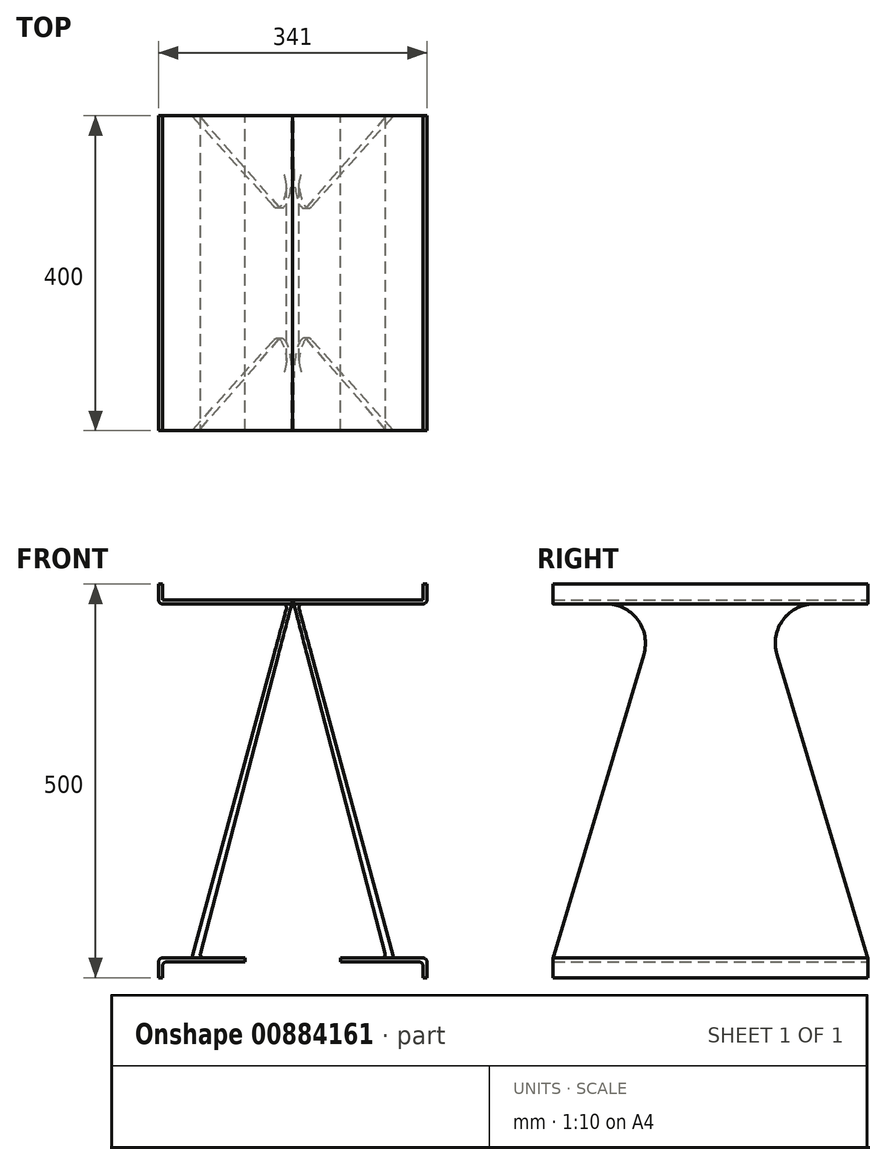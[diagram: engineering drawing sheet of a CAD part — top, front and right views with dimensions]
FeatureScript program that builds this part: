
annotation { "Feature Type Name" : "Feature", "Feature Type Description" : "" }
export const myFeature = defineFeature(function(context is Context, id is Id, definition is map)
    precondition{}
    {
        {
            var Q0;
            Q0=qCreatedBy(makeId("Front.planeOp"),FACE);
            var sketch = newSketch(context, id + "F0", { "sketchPlane" : qUnion([Q0])});
            skLineSegment(sketch, "E0", {"start": v(0, 0) * mm, "end": v(-170.5, 0) * mm, "construction": true});
            skLineSegment(sketch, "E1", {"start": v(-170.5, 0) * mm, "end": v(-170.5, -500) * mm, "construction": true});
            skLineSegment(sketch, "E2", {"start": v(-170.5, -500) * mm, "end": v(0, -500) * mm, "construction": true});
            skLineSegment(sketch, "E3", {"start": v(0, -500) * mm, "end": v(0, 0) * mm, "construction": true});
            skLineSegment(sketch, "E4.MirrorCS", {"start": v(0, 0) * mm, "end": v(170.5, 0) * mm, "construction": true});
            skLineSegment(sketch, "E5.MirrorCS", {"start": v(170.5, 0) * mm, "end": v(170.5, -500) * mm, "construction": true});
            skLineSegment(sketch, "E6.MirrorCS", {"start": v(170.5, -500) * mm, "end": v(0, -500) * mm, "construction": true});
            skLineSegment(sketch, "E7", {"start": v(170.5, -500) * mm, "end": v(0, 0) * mm});
            skLineSegment(sketch, "E8.0", {"start": v(165.77, -501.61) * mm, "end": v(0, -15.5) * mm});
            skLineSegment(sketch, "E9.0", {"start": v(0, -20) * mm, "end": v(-170.5, -20) * mm, "construction": true});
            skLineSegment(sketch, "E10.0", {"start": v(-165.5, 0) * mm, "end": v(-165.5, -500) * mm, "construction": true});
            skLineSegment(sketch, "E11.0", {"start": v(0, -25) * mm, "end": v(-170.5, -25) * mm, "construction": true});
            skLineSegment(sketch, "E12.0", {"start": v(-125.5, 0) * mm, "end": v(-125.5, -500) * mm, "construction": true});
            skLineSegment(sketch, "E13", {"start": v(0, -20) * mm, "end": v(-125.5, -500) * mm, "construction": true});
            skSolve(sketch);
        }
        {
            var Q0;
            Q0=qCreatedBy(makeId("Front.planeOp"),FACE);
            var sketch = newSketch(context, id + "F1", { "sketchPlane" : qUnion([Q0])});
            skLineSegment(sketch, "E14.2", {"start": v(0, -20) * mm, "end": v(-165.5, -20) * mm});
            skLineSegment(sketch, "E14.4", {"start": v(-165.5, 0) * mm, "end": v(-165.5, -20) * mm});
            skLineSegment(sketch, "E14.5", {"start": v(-170.5, 0) * mm, "end": v(-170.5, -25) * mm});
            skPoint(sketch, "E15.orphan", {"position": v(0, -20) * mm});
            skPoint(sketch, "E16.orphan", {"position": v(0, -25) * mm});
            skPoint(sketch, "E17.orphan", {"position": v(-170.5, -20) * mm});
            skLineSegment(sketch, "E18", {"start": v(-170.5, 0) * mm, "end": v(-165.5, 0) * mm});
            skPoint(sketch, "E19.orphan", {"position": v(-170.5, -500) * mm});
            skLineSegment(sketch, "E20.0", {"start": v(0, -20) * mm, "end": v(-118.96, -475) * mm});
            skLineSegment(sketch, "E21.0", {"start": v(-165.5, -480) * mm, "end": v(-60.5, -480) * mm});
            skLineSegment(sketch, "E22.0", {"start": v(-170.5, -500) * mm, "end": v(-165.5, -500) * mm});
            skLineSegment(sketch, "E23.trimOffspring", {"start": v(-6.46, -25) * mm, "end": v(-170.5, -25) * mm});
            skLineSegment(sketch, "E24.trimOffspring", {"start": v(-6.46, -25) * mm, "end": v(-128.05, -475) * mm});
            skLineSegment(sketch, "E25", {"start": v(-170.5, -500) * mm, "end": v(-170.5, -475) * mm});
            skPoint(sketch, "E26.orphan", {"position": v(-165.5, -500) * mm});
            skLineSegment(sketch, "E27.0", {"start": v(-170.5, -475) * mm, "end": v(-128.05, -475) * mm});
            skPoint(sketch, "E28.orphan", {"position": v(0, -500) * mm});
            skLineSegment(sketch, "E29.trimOffspring", {"start": v(-165.5, -480) * mm, "end": v(-165.5, -500) * mm});
            skPoint(sketch, "E30.orphan", {"position": v(-125.5, -500) * mm});
            skLineSegment(sketch, "E31.0", {"start": v(-170.5, -500) * mm, "end": v(-165.5, -500) * mm, "construction": true});
            skLineSegment(sketch, "E32.1", {"start": v(-60.5, -475) * mm, "end": v(-60.5, -480) * mm});
            skLineSegment(sketch, "E33.trimOffspring", {"start": v(-118.96, -475) * mm, "end": v(-60.5, -475) * mm});
            skLineSegment(sketch, "E34", {"start": v(0, -20) * mm, "end": v(0, -35.48) * mm, "construction": true});
            skLineSegment(sketch, "E35", {"start": v(-170.5, -25) * mm, "end": v(-170.5, -475) * mm, "construction": true});
            skSolve(sketch);
        }
        {
            var Q0;
            Q0 = qSketchRegion(id + "F1", true);
            extrude(context, id + "F2", {"entities" : qUnion([Q0]), "depth" : 400 * mm, "offsetDistance" : 25 * mm});
        }
        {
            var Q0;
            Q0=qCreatedBy(makeId("Right.planeOp"),FACE);
            var sketch = newSketch(context, id + "F3", { "sketchPlane" : qUnion([Q0])});
            skLineSegment(sketch, "E36.0", {"start": v(-400, -25) * mm, "end": v(0, -25) * mm, "construction": true});
            skLineSegment(sketch, "E36.1", {"start": v(-400, -475) * mm, "end": v(0, -475) * mm, "construction": true});
            skLineSegment(sketch, "E37", {"start": v(-200, -25) * mm, "end": v(-200, -475) * mm, "construction": true});
            skLineSegment(sketch, "E38", {"start": v(-200, -250) * mm, "end": v(135.97, -250) * mm, "construction": true});
            skLineSegment(sketch, "E39", {"start": v(0, -25) * mm, "end": v(-132.5, -250) * mm});
            skLineSegment(sketch, "E40", {"start": v(-132.5, -250) * mm, "end": v(0, -475) * mm});
            skLineSegment(sketch, "E41.MirrorCS", {"start": v(-400, -25) * mm, "end": v(-267.5, -250) * mm});
            skLineSegment(sketch, "E42.MirrorCS", {"start": v(-267.5, -250) * mm, "end": v(-400, -475) * mm});
            skLineSegment(sketch, "E43", {"start": v(0, -25) * mm, "end": v(162.07, -25) * mm});
            skLineSegment(sketch, "E44", {"start": v(162.07, -25) * mm, "end": v(162.07, -475) * mm});
            skLineSegment(sketch, "E45", {"start": v(162.07, -475) * mm, "end": v(0, -475) * mm});
            skLineSegment(sketch, "E46.MirrorCS", {"start": v(-400, -25) * mm, "end": v(-562.07, -25) * mm});
            skLineSegment(sketch, "E47.MirrorCS", {"start": v(-562.07, -475) * mm, "end": v(-400, -475) * mm});
            skLineSegment(sketch, "E48.MirrorCS", {"start": v(-562.07, -25) * mm, "end": v(-562.07, -475) * mm});
            skSolve(sketch);
        }
        {
            var Q0;
            Q0=qCreatedBy(makeId("Right.planeOp"),FACE);
            var sketch = newSketch(context, id + "F4", { "sketchPlane" : qUnion([Q0])});
            skLineSegment(sketch, "E49", {"start": v(-400, -475) * mm, "end": v(-265.3, -25) * mm});
            skLineSegment(sketch, "E50", {"start": v(-511.72, -25) * mm, "end": v(-492.62, -475) * mm});
            skLineSegment(sketch, "E51", {"start": v(-492.62, -475) * mm, "end": v(-400, -475) * mm});
            skLineSegment(sketch, "E52.0", {"start": v(-200, -25) * mm, "end": v(-200, -475) * mm, "construction": true});
            skLineSegment(sketch, "E53.MirrorCS", {"start": v(0, -475) * mm, "end": v(-134.7, -25) * mm});
            skLineSegment(sketch, "E54.MirrorCS", {"start": v(111.72, -25) * mm, "end": v(92.62, -475) * mm});
            skLineSegment(sketch, "E55.MirrorCS", {"start": v(92.62, -475) * mm, "end": v(0, -475) * mm});
            skLineSegment(sketch, "E56.0", {"start": v(-400, -25) * mm, "end": v(-265.3, -25) * mm});
            skLineSegment(sketch, "E57", {"start": v(0, -25) * mm, "end": v(111.72, -25) * mm});
            skPoint(sketch, "E58.orphan", {"position": v(111.45, -31.3) * mm});
            skLineSegment(sketch, "E59.MirrorCS", {"start": v(-400, -25) * mm, "end": v(-511.72, -25) * mm});
            skPoint(sketch, "E60.orphan", {"position": v(-511.45, -31.3) * mm});
            skPoint(sketch, "E61.orphan", {"position": v(-132.82, -31.3) * mm});
            skPoint(sketch, "E62.orphan", {"position": v(-267.18, -31.3) * mm});
            skLineSegment(sketch, "E63.trimOffspring", {"start": v(-134.7, -25) * mm, "end": v(0, -25) * mm});
            skPoint(sketch, "E64.orphan", {"position": v(0, -475) * mm});
            skSolve(sketch);
        }
        {
            var Q0;
            Q0 = qSketchRegion(id + "F4", true);
            extrude(context, id + "F5", {"entities" : qUnion([Q0]), "operationType" : NewBodyOperationType.REMOVE, "oppositeDirection" : true, "depth" : 333 * mm, "offsetDistance" : 25 * mm});
        }
        {
            var Q0;
            Q0=makeQuery(id+"F5.boolean.opBoolean","INTERSECT",EDGE,{"derivedFrom":[makeQuery(id+"F5.opExtrude","SWEPT_FACE",FACE,{"disambiguationData":[OSD([sQuery(id+"F4.wireOp",EDGE,"E56.0"),sQuery(id+"F4.wireOp",EDGE,"E59.MirrorCS")])]}),makeQuery(id+"F5.opExtrude","SWEPT_FACE",FACE,{"disambiguationData":[OSD([sQuery(id+"F4.wireOp",EDGE,"E57"),sQuery(id+"F4.wireOp",EDGE,"E63.trimOffspring")])]})]});
            var Q1;
            Q1=makeQuery(id+"F2.opExtrude","SWEPT_EDGE",EDGE,{"disambiguationData":[OSD([sQuery(id+"F1.wireOp",EDGE,"E23.trimOffspring"),sQuery(id+"F1.wireOp",EDGE,"E24.trimOffspring")])]});
            var Q2;
            Q2=makeQuery(id+"F2.opExtrude","SWEPT_EDGE",EDGE,{"disambiguationData":[OSD([sQuery(id+"F1.wireOp",EDGE,"E25"),sQuery(id+"F1.wireOp",EDGE,"E27.0")])]});
            var Q3;
            Q3=makeQuery(id+"F2.opExtrude","SWEPT_EDGE",EDGE,{"disambiguationData":[OSD([sQuery(id+"F1.wireOp",EDGE,"E21.0"),sQuery(id+"F1.wireOp",EDGE,"E29.trimOffspring")])]});
            var Q4;
            Q4=makeQuery(id+"F2.opExtrude","SWEPT_EDGE",EDGE,{"disambiguationData":[OSD([sQuery(id+"F1.wireOp",EDGE,"E24.trimOffspring"),sQuery(id+"F1.wireOp",EDGE,"E27.0")])]});
            var Q5;
            Q5=makeQuery(id+"F2.opExtrude","SWEPT_EDGE",EDGE,{"disambiguationData":[OSD([sQuery(id+"F1.wireOp",EDGE,"E20.0"),sQuery(id+"F1.wireOp",EDGE,"E33.trimOffspring")])]});
            fillet(context, id + "F6", {"entities" : qUnion([Q0, Q1, Q2, Q3, Q4, Q5]), "radius" : 5 * mm, "tangentPropagation" : true, "allowEdgeOverflow" : false});
        }
        {
            var Q0;
            Q0=makeQuery(id+"F5.boolean.opBoolean","COPY",EDGE,{"derivedFrom":makeQuery(id+"F5.opExtrude","SWEPT_EDGE",EDGE,{"disambiguationData":[OSD([sQuery(id+"F4.wireOp",EDGE,"E53.MirrorCS"),sQuery(id+"F4.wireOp",EDGE,"E63.trimOffspring")])]})});
            var Q1;
            Q1=makeQuery(id+"F5.boolean.opBoolean","COPY",EDGE,{"derivedFrom":makeQuery(id+"F5.opExtrude","SWEPT_EDGE",EDGE,{"disambiguationData":[OSD([sQuery(id+"F4.wireOp",EDGE,"E49"),sQuery(id+"F4.wireOp",EDGE,"E56.0")])]})});
            fillet(context, id + "F7", {"entities" : qUnion([Q0, Q1]), "radius" : 50 * mm, "tangentPropagation" : true, "allowEdgeOverflow" : false});
        }
        {
            var Q0;
            Q0=makeQuery(id+"F2.opExtrude","SWEPT_BODY",BODY,{"disambiguationData":[OSD([sQuery(id+"F1.wireOp",EDGE,"E14.2"),sQuery(id+"F1.wireOp",EDGE,"E14.5"),sQuery(id+"F1.wireOp",EDGE,"E18"),sQuery(id+"F1.wireOp",EDGE,"E20.0"),sQuery(id+"F1.wireOp",EDGE,"E21.0"),sQuery(id+"F1.wireOp",EDGE,"E23.trimOffspring"),sQuery(id+"F1.wireOp",EDGE,"E24.trimOffspring"),sQuery(id+"F1.wireOp",EDGE,"E25"),sQuery(id+"F1.wireOp",EDGE,"E27.0"),sQuery(id+"F1.wireOp",EDGE,"E14.4"),sQuery(id+"F1.wireOp",EDGE,"E29.trimOffspring"),sQuery(id+"F1.wireOp",EDGE,"E22.0"),sQuery(id+"F1.wireOp",EDGE,"E32.1"),sQuery(id+"F1.wireOp",EDGE,"E33.trimOffspring")])]});
            var Q1;
            Q1=qCreatedBy(makeId("Right.planeOp"),FACE);
            mirror(context, id + "F8", {"entities" : qUnion([Q0]), "mirrorPlane" : qUnion([Q1])});
        }
    });
